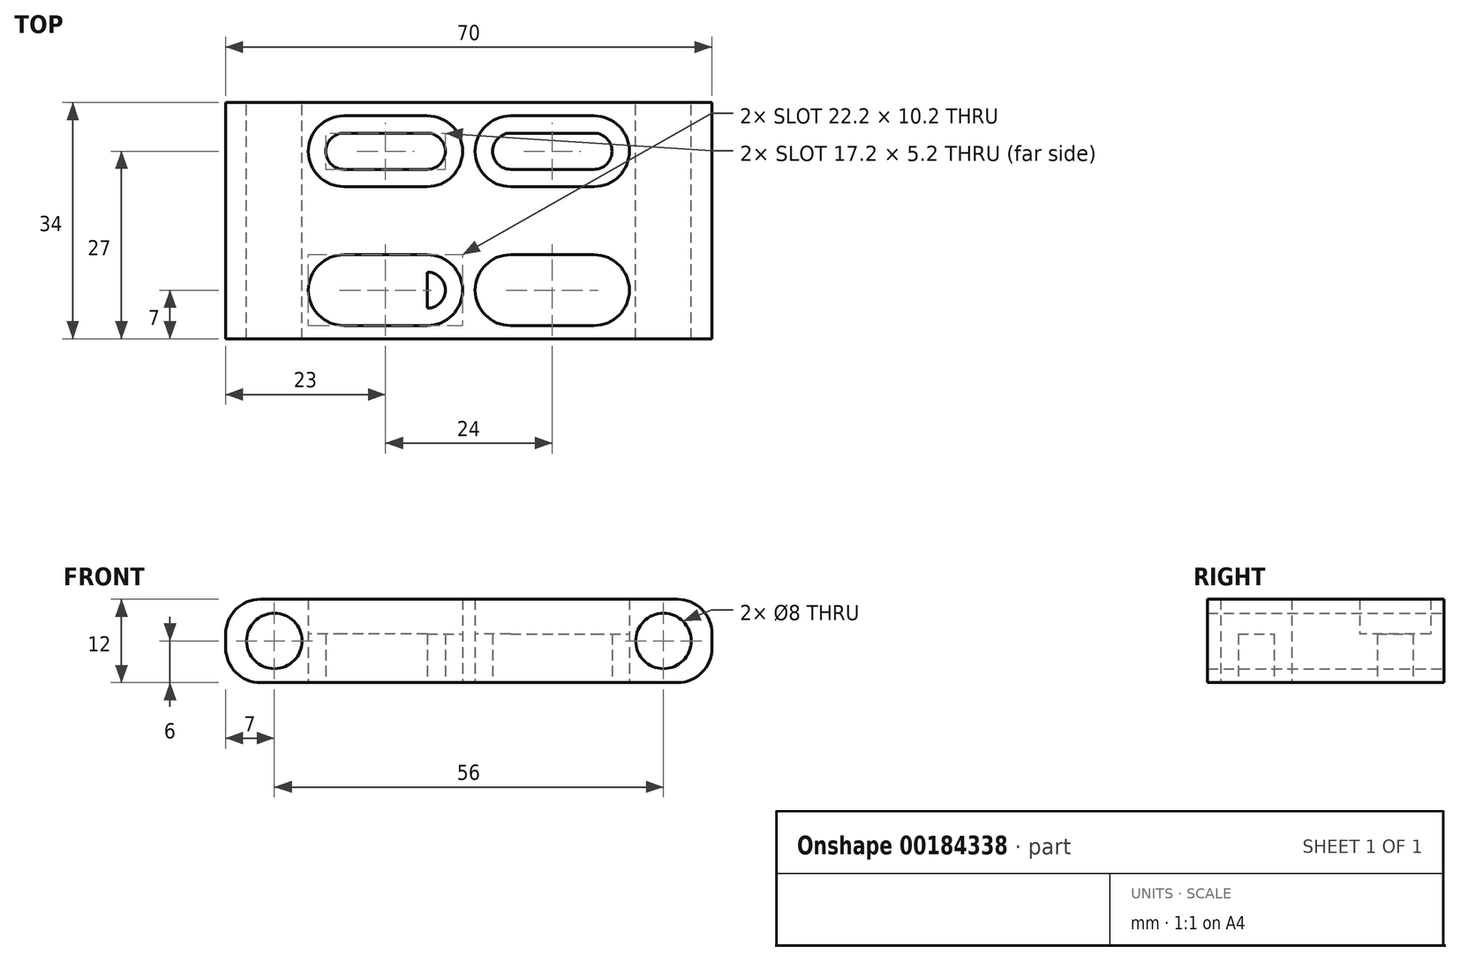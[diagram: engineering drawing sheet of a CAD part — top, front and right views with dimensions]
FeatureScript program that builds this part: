
annotation { "Feature Type Name" : "Feature", "Feature Type Description" : "" }
export const myFeature = defineFeature(function(context is Context, id is Id, definition is map)
    precondition{}
    {
        {
            var Q0;
            Q0=qCreatedBy(makeId("Top.planeOp"),FACE);
            var sketch = newSketch(context, id + "F0", { "sketchPlane" : qUnion([Q0])});
            skLineSegment(sketch, "E0.bottom", {"start": v(35, 17) * mm, "end": v(-35, 17) * mm});
            skLineSegment(sketch, "E0.top", {"start": v(35, -17) * mm, "end": v(-35, -17) * mm});
            skLineSegment(sketch, "E0.left", {"start": v(35, 17) * mm, "end": v(35, -17) * mm});
            skLineSegment(sketch, "E0.right", {"start": v(-35, 17) * mm, "end": v(-35, -17) * mm});
            skPoint(sketch, "E0.middle", {"position": v(0, 0) * mm});
            skLineSegment(sketch, "E1.bottom", {"start": v(-6, 12.6) * mm, "end": v(-18, 12.6) * mm});
            skLineSegment(sketch, "E1.top", {"start": v(-6, 7.4) * mm, "end": v(-18, 7.4) * mm});
            skLineSegment(sketch, "E1.left", {"start": v(-6, 12.6) * mm, "end": v(-6, 7.4) * mm});
            skLineSegment(sketch, "E1.right", {"start": v(-18, 12.6) * mm, "end": v(-18, 7.4) * mm});
            skPoint(sketch, "E1.middle", {"position": v(-12, 10) * mm});
            skArc(sketch, "E2", {"start": v(-6, 7.4) * mm, "mid": v(-3.4, 10) * mm, "end": v(-6, 12.6) * mm});
            skArc(sketch, "E3", {"start": v(-18, 12.6) * mm, "mid": v(-20.6, 10) * mm, "end": v(-18, 7.4) * mm});
            skLineSegment(sketch, "E4.MirrorCS", {"start": v(6, 12.6) * mm, "end": v(6, 7.4) * mm});
            skLineSegment(sketch, "E5.MirrorCS", {"start": v(18, 12.6) * mm, "end": v(18, 7.4) * mm});
            skLineSegment(sketch, "E6.MirrorCS", {"start": v(6, 7.4) * mm, "end": v(18, 7.4) * mm});
            skLineSegment(sketch, "E7.MirrorCS", {"start": v(6, 12.6) * mm, "end": v(18, 12.6) * mm});
            skArc(sketch, "E8.MirrorCS", {"start": v(6, 7.4) * mm, "mid": v(3.4, 10) * mm, "end": v(6, 12.6) * mm});
            skPoint(sketch, "E9.MirrorP", {"position": v(12, 10) * mm});
            skArc(sketch, "E10.MirrorCS", {"start": v(18, 12.6) * mm, "mid": v(20.6, 10) * mm, "end": v(18, 7.4) * mm});
            skLineSegment(sketch, "E11.MirrorCS", {"start": v(-18, -12.6) * mm, "end": v(-18, -7.4) * mm});
            skLineSegment(sketch, "E12.MirrorCS", {"start": v(6, -12.6) * mm, "end": v(6, -7.4) * mm});
            skLineSegment(sketch, "E13.MirrorCS", {"start": v(-6, -12.6) * mm, "end": v(-6, -7.4) * mm});
            skLineSegment(sketch, "E14.MirrorCS", {"start": v(18, -12.6) * mm, "end": v(18, -7.4) * mm});
            skLineSegment(sketch, "E15.MirrorCS", {"start": v(-6, -12.6) * mm, "end": v(-18, -12.6) * mm});
            skArc(sketch, "E16.MirrorCS", {"start": v(6, -7.4) * mm, "mid": v(3.4, -10) * mm, "end": v(6, -12.6) * mm});
            skArc(sketch, "E17.MirrorCS", {"start": v(-6, -7.4) * mm, "mid": v(-3.4, -10) * mm, "end": v(-6, -12.6) * mm});
            skPoint(sketch, "E18.MirrorP", {"position": v(12, -10) * mm});
            skArc(sketch, "E19.MirrorCS", {"start": v(-18, -12.6) * mm, "mid": v(-20.6, -10) * mm, "end": v(-18, -7.4) * mm});
            skLineSegment(sketch, "E20.MirrorCS", {"start": v(-6, -7.4) * mm, "end": v(-18, -7.4) * mm});
            skLineSegment(sketch, "E21.MirrorCS", {"start": v(6, -7.4) * mm, "end": v(18, -7.4) * mm});
            skLineSegment(sketch, "E22.MirrorCS", {"start": v(6, -12.6) * mm, "end": v(18, -12.6) * mm});
            skPoint(sketch, "E23.MirrorP", {"position": v(-12, -10) * mm});
            skArc(sketch, "E24.MirrorCS", {"start": v(18, -12.6) * mm, "mid": v(20.6, -10) * mm, "end": v(18, -7.4) * mm});
            skLineSegment(sketch, "E25.0", {"start": v(-6, 15.1) * mm, "end": v(-18, 15.1) * mm});
            skArc(sketch, "E25.1", {"start": v(-6, 4.9) * mm, "mid": v(-0.9, 10) * mm, "end": v(-6, 15.1) * mm});
            skLineSegment(sketch, "E25.2", {"start": v(-6, 4.9) * mm, "end": v(-18, 4.9) * mm});
            skArc(sketch, "E25.3", {"start": v(-18, 15.1) * mm, "mid": v(-23.1, 10) * mm, "end": v(-18, 4.9) * mm});
            skLineSegment(sketch, "E26.0", {"start": v(6, 15.1) * mm, "end": v(18, 15.1) * mm});
            skArc(sketch, "E26.1", {"start": v(6, 4.9) * mm, "mid": v(0.9, 10) * mm, "end": v(6, 15.1) * mm});
            skLineSegment(sketch, "E26.2", {"start": v(6, 4.9) * mm, "end": v(18, 4.9) * mm});
            skArc(sketch, "E26.3", {"start": v(18, 15.1) * mm, "mid": v(23.1, 10) * mm, "end": v(18, 4.9) * mm});
            skArc(sketch, "E27.0", {"start": v(-18, -15.1) * mm, "mid": v(-23.1, -10) * mm, "end": v(-18, -4.9) * mm});
            skLineSegment(sketch, "E27.1", {"start": v(-6, -15.1) * mm, "end": v(-18, -15.1) * mm});
            skArc(sketch, "E27.2", {"start": v(-6, -4.9) * mm, "mid": v(-0.9, -10) * mm, "end": v(-6, -15.1) * mm});
            skLineSegment(sketch, "E27.3", {"start": v(-6, -4.9) * mm, "end": v(-18, -4.9) * mm});
            skLineSegment(sketch, "E28.0", {"start": v(6, -4.9) * mm, "end": v(18, -4.9) * mm});
            skArc(sketch, "E28.1", {"start": v(6, -4.9) * mm, "mid": v(0.9, -10) * mm, "end": v(6, -15.1) * mm});
            skLineSegment(sketch, "E28.2", {"start": v(6, -15.1) * mm, "end": v(18, -15.1) * mm});
            skArc(sketch, "E28.3", {"start": v(18, -15.1) * mm, "mid": v(23.1, -10) * mm, "end": v(18, -4.9) * mm});
            skSolve(sketch);
        }
        {
            var Q0;
            Q0=makeQuery(id+"F0.imprint","IMPRINT",FACE,{"disambiguationData":[TD([[makeQuery(id+"F0.imprint","IMPRINT",EDGE,{"derivedFrom":sQuery(id+"F0.wireOp",EDGE,"E0.bottom")}),1.0]])]});
            extrude(context, id + "F1", {"entities" : qUnion([Q0]), "depth" : 12 * mm, "offsetDistance" : 25 * mm});
        }
        {
            var Q0;
            Q0=makeQuery(id+"F0.imprint","IMPRINT",FACE,{"disambiguationData":[TD([[makeQuery(id+"F0.imprint","IMPRINT",EDGE,{"derivedFrom":sQuery(id+"F0.wireOp",EDGE,"E1.top")}),1.0]])]});
            var Q1;
            Q1=makeQuery(id+"F0.imprint","IMPRINT",FACE,{"disambiguationData":[TD([[makeQuery(id+"F0.imprint","IMPRINT",EDGE,{"derivedFrom":sQuery(id+"F0.wireOp",EDGE,"E6.MirrorCS")}),-1.0]])]});
            var Q2;
            Q2=makeQuery(id+"F0.imprint","IMPRINT",FACE,{"disambiguationData":[TD([[makeQuery(id+"F0.imprint","IMPRINT",EDGE,{"derivedFrom":sQuery(id+"F0.wireOp",EDGE,"E24.MirrorCS")}),-1.0]])]});
            var Q3;
            Q3=makeQuery(id+"F0.imprint","IMPRINT",FACE,{"disambiguationData":[TD([[makeQuery(id+"F0.imprint","IMPRINT",EDGE,{"derivedFrom":sQuery(id+"F0.wireOp",EDGE,"E17.MirrorCS")}),1.0]])]});
            extrude(context, id + "F2", {"entities" : qUnion([Q0, Q1, Q2, Q3]), "operationType" : NewBodyOperationType.ADD, "depth" : 7 * mm, "offsetDistance" : 25 * mm});
        }
        {
            var Q0;
            Q0=makeQuery(id+"F1.opExtrude","SWEPT_FACE",FACE,{"disambiguationData":[OSD([sQuery(id+"F0.wireOp",EDGE,"E0.bottom")])]});
            var sketch = newSketch(context, id + "F3", { "sketchPlane" : qUnion([Q0])});
            skCircle(sketch, "E29", {"center": v(28, 6) * mm, "radius": 4 * mm});
            skPoint(sketch, "E29.centerSnap0", {"position": v(35, 6) * mm});
            skCircle(sketch, "E30.MirrorC", {"center": v(-28, 6) * mm, "radius": 4 * mm});
            skSolve(sketch);
        }
        {
            var Q0;
            Q0 = qSketchRegion(id + "F3", true);
            var Q1;
            Q1=makeQuery(id+"F3.imprint","IMPRINT",FACE,{"disambiguationData":[TD([[makeQuery(id+"F3.imprint","IMPRINT",EDGE,{"derivedFrom":sQuery(id+"F3.wireOp",EDGE,"vND7AFlF-akzp-ENS0-NY0I-yX4vnQVuRvYD")}),1.0]])]});
            var Q2;
            Q2=makeQuery(id+"F3.imprint","IMPRINT",FACE,{"disambiguationData":[TD([[makeQuery(id+"F3.imprint","IMPRINT",EDGE,{"derivedFrom":sQuery(id+"F3.wireOp",EDGE,"5ViJzZHK-Zty9-BKOm-1Nwi-lptIeARjUbZl")}),1.0]])]});
            extrude(context, id + "F4", {"entities" : qUnion([Q0, Q1, Q2]), "operationType" : NewBodyOperationType.REMOVE, "endBound" : BoundingType.THROUGH_ALL, "oppositeDirection" : true, "depth" : 25 * mm, "offsetDistance" : 25 * mm});
        }
        {
            var Q0;
            Q0=makeQuery(id+"F1.opExtrude","CAP_EDGE",EDGE,{"disambiguationData":[OSD([sQuery(id+"F0.wireOp",EDGE,"E0.right")])],"isStart":false});
            var Q1;
            Q1=makeQuery(id+"F1.opExtrude","CAP_EDGE",EDGE,{"disambiguationData":[OSD([sQuery(id+"F0.wireOp",EDGE,"E0.left")])],"isStart":false});
            var Q2;
            Q2=makeQuery(id+"F1.opExtrude","CAP_EDGE",EDGE,{"disambiguationData":[OSD([sQuery(id+"F0.wireOp",EDGE,"E0.right")])],"isStart":true});
            var Q3;
            Q3=makeQuery(id+"F1.opExtrude","CAP_EDGE",EDGE,{"disambiguationData":[OSD([sQuery(id+"F0.wireOp",EDGE,"E0.left")])],"isStart":true});
            fillet(context, id + "F5", {"entities" : qUnion([Q0, Q1, Q2, Q3]), "tangentPropagation" : true, "radius" : 5 * mm, "defaultsChanged" : false, "vertexSettings" : [], "allowEdgeOverflow" : false});
        }
    });
